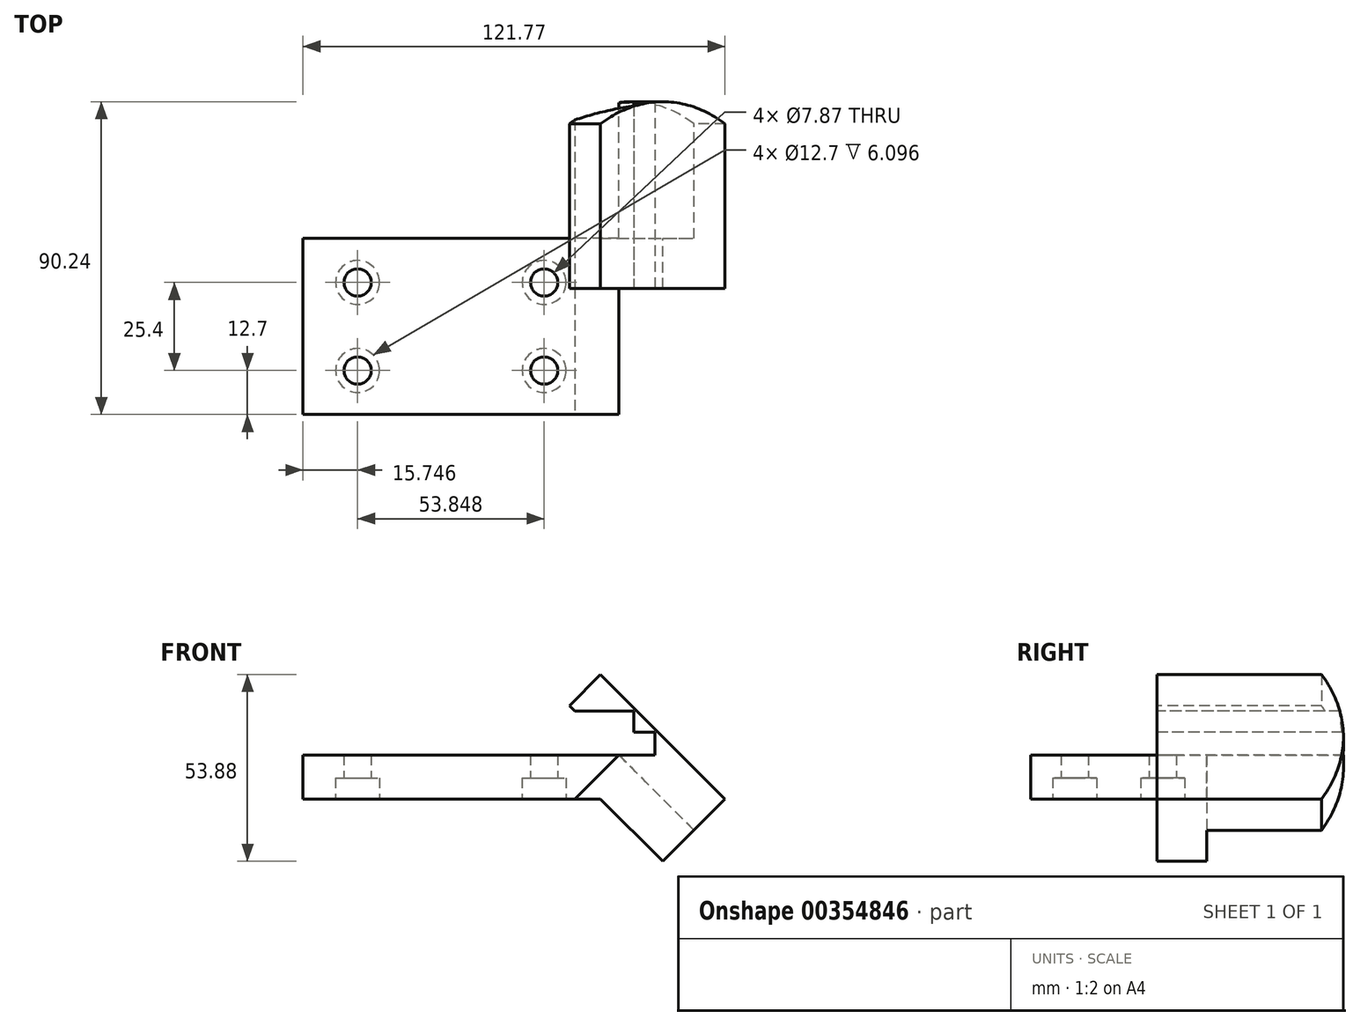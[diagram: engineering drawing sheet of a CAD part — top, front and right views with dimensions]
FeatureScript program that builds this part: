
annotation { "Feature Type Name" : "Feature", "Feature Type Description" : "" }
export const myFeature = defineFeature(function(context is Context, id is Id, definition is map)
    precondition{}
    {
        {
            var Q0;
            Q0=qCreatedBy(makeId("Front.planeOp"),FACE);
            var sketch = newSketch(context, id + "F0", { "sketchPlane" : qUnion([Q0])});
            skLineSegment(sketch, "E0.bottom", {"start": v(0, 0) * mm, "end": v(-85.85, 0) * mm});
            skLineSegment(sketch, "E0.top", {"start": v(5.26, 12.7) * mm, "end": v(-85.85, 12.7) * mm});
            skLineSegment(sketch, "E0.right", {"start": v(-85.85, 0) * mm, "end": v(-85.85, 12.7) * mm});
            skLineSegment(sketch, "E1", {"start": v(5.26, 12.7) * mm, "end": v(54.83, -36.87) * mm});
            skLineSegment(sketch, "E2", {"start": v(0, 0) * mm, "end": v(45.85, -45.85) * mm});
            skLineSegment(sketch, "E3", {"start": v(54.83, -36.87) * mm, "end": v(45.85, -45.85) * mm});
            skSolve(sketch);
        }
        {
            var Q0;
            Q0 = qSketchRegion(id + "F0", true);
            extrude(context, id + "F1", {"entities" : qUnion([Q0]), "endBound" : BoundingType.SYMMETRIC, "depth" : 50.8 * mm});
        }
        {
            var Q0;
            Q0=makeQuery(id+"F1.opExtrude","SWEPT_FACE",FACE,{"disambiguationData":[OSD([sQuery(id+"F0.wireOp",EDGE,"E0.bottom")])]});
            var sketch = newSketch(context, id + "F2", { "sketchPlane" : qUnion([Q0])});
            skPoint(sketch, "E4", {"position": v(-70.1, 12.7) * mm});
            skPoint(sketch, "E5.0.1.0", {"position": v(-70.1, -12.7) * mm});
            skPoint(sketch, "E5.1.0.0", {"position": v(-16.26, 12.7) * mm});
            skPoint(sketch, "E5.1.1.0", {"position": v(-16.26, -12.7) * mm});
            skLineSegment(sketch, "E5.direction1", {"start": v(-70.1, 12.7) * mm, "end": v(-16.26, 12.7) * mm, "construction": true});
            skLineSegment(sketch, "E5.direction2", {"start": v(-70.1, 12.7) * mm, "end": v(-70.1, -12.7) * mm, "construction": true});
            skSolve(sketch);
        }
        {
            var Q0;
            Q0=sQuery(id+"F2.wireOp",VERTEX,"E4");
            var Q1;
            Q1=sQuery(id+"F2.wireOp",VERTEX,"E5.1.0.0");
            var Q2;
            Q2=sQuery(id+"F2.wireOp",VERTEX,"E5.1.1.0");
            var Q3;
            Q3=sQuery(id+"F2.wireOp",VERTEX,"E5.0.1.0");
            var Q4;
            Q4=makeQuery(id+"F1.opExtrude","SWEPT_BODY",BODY,{"disambiguationData":[OSD([sQuery(id+"F0.wireOp",EDGE,"E0.bottom"),sQuery(id+"F0.wireOp",EDGE,"E0.top"),sQuery(id+"F0.wireOp",EDGE,"E0.right"),sQuery(id+"F0.wireOp",EDGE,"E1"),sQuery(id+"F0.wireOp",EDGE,"E2"),sQuery(id+"F0.wireOp",EDGE,"E3")])]});
            hole(context, id + "F3", {"style" : HoleStyle.C_BORE, "endStyle" : HoleEndStyle.THROUGH, "holeDiameter" : 7.87 * mm, "cBoreDiameter" : 12.7 * mm, "cBoreDepth" : 6.1 * mm, "isTappedThrough" : true, "tappedDepth" : 12.7 * mm, "tapClearance" : 3, "startFromSketch" : true, "locations" : qUnion([Q0, Q1, Q2, Q3]), "scope" : qUnion([Q4])});
        }
        {
            var Q0;
            Q0=makeQuery(id+"F1.opExtrude","SWEPT_FACE",FACE,{"disambiguationData":[OSD([sQuery(id+"F0.wireOp",EDGE,"E1")])]});
            var sketch = newSketch(context, id + "F4", { "sketchPlane" : qUnion([Q0])});
            skArc(sketch, "E6", {"start": v(58.48, -25.4) * mm, "mid": v(64.84, 0) * mm, "end": v(58.48, 25.4) * mm});
            skLineSegment(sketch, "E7.0.0", {"start": v(58.48, 25.4) * mm, "end": v(11, 25.4) * mm});
            skLineSegment(sketch, "E7.0.1", {"start": v(-5.26, 25.4) * mm, "end": v(-5.26, -25.4) * mm});
            skLineSegment(sketch, "E7.0.2", {"start": v(11, -25.4) * mm, "end": v(58.48, -25.4) * mm});
            skPoint(sketch, "E8.orphan", {"position": v(64.84, 25.4) * mm});
            skPoint(sketch, "E9.orphan", {"position": v(64.84, -25.4) * mm});
            skLineSegment(sketch, "E10", {"start": v(11, 25.4) * mm, "end": v(11, -25.4) * mm});
            skSolve(sketch);
        }
        {
            var Q0;
            Q0 = qSketchRegion(id + "F4", true);
            extrude(context, id + "F5", {"entities" : qUnion([Q0]), "operationType" : NewBodyOperationType.ADD, "depth" : 12.7 * mm});
        }
        {
            var Q0;
            {var subQ0=sQuery(id+"F0.wireOp",EDGE,"E1");var subQ1=makeQuery(id+"F1.opExtrude","SWEPT_FACE",FACE,{"disambiguationData":[OSD([subQ0])]});var subQ2=sQuery(id+"F0.wireOp",EDGE,"E3");Q0=makeQuery(id+"F5.boolean.opBoolean","SPLIT",FACE,{"disambiguationData":[TD([makeQuery(id+"F1.opExtrude","CAP_FACE",FACE,{"disambiguationData":[OSD([sQuery(id+"F0.wireOp",EDGE,"E0.bottom"),sQuery(id+"F0.wireOp",EDGE,"E0.top"),sQuery(id+"F0.wireOp",EDGE,"E0.right"),subQ0,sQuery(id+"F0.wireOp",EDGE,"E2"),subQ2])],"isStart":false}),subQ1,makeQuery(id+"F1.opExtrude","SWEPT_FACE",FACE,{"disambiguationData":[OSD([subQ2])]}),makeQuery(id+"F5.opExtrude","SWEPT_FACE",FACE,{"disambiguationData":[OSD([sQuery(id+"F4.wireOp",EDGE,"E6")])]}),makeQuery(id+"F5.opExtrude","SWEPT_FACE",FACE,{"disambiguationData":[OSD([sQuery(id+"F4.wireOp",EDGE,"E7.0.2")])]})])],"derivedFrom":subQ1});}
            var Q1;
            {var subQ0=sQuery(id+"F0.wireOp",EDGE,"E3");var subQ1=sQuery(id+"F0.wireOp",EDGE,"E1");var subQ2=makeQuery(id+"F1.opExtrude","SWEPT_FACE",FACE,{"disambiguationData":[OSD([subQ1])]});Q1=makeQuery(id+"F5.boolean.opBoolean","SPLIT",FACE,{"disambiguationData":[TD([makeQuery(id+"F1.opExtrude","CAP_FACE",FACE,{"disambiguationData":[OSD([sQuery(id+"F0.wireOp",EDGE,"E0.bottom"),sQuery(id+"F0.wireOp",EDGE,"E0.top"),sQuery(id+"F0.wireOp",EDGE,"E0.right"),subQ1,sQuery(id+"F0.wireOp",EDGE,"E2"),subQ0])],"isStart":true}),subQ2,makeQuery(id+"F1.opExtrude","SWEPT_FACE",FACE,{"disambiguationData":[OSD([subQ0])]}),makeQuery(id+"F5.opExtrude","SWEPT_FACE",FACE,{"disambiguationData":[OSD([sQuery(id+"F4.wireOp",EDGE,"E6")])]}),makeQuery(id+"F5.opExtrude","SWEPT_FACE",FACE,{"disambiguationData":[OSD([sQuery(id+"F4.wireOp",EDGE,"E7.0.0")])]})])],"derivedFrom":subQ2});}
            extrude(context, id + "F6", {"entities" : qUnion([Q0, Q1]), "operationType" : NewBodyOperationType.REMOVE, "endBound" : BoundingType.THROUGH_ALL, "oppositeDirection" : true, "depth" : 25.4 * mm});
        }
        {
            var Q0;
            Q0=makeQuery(id+"F5.opExtrude","SWEPT_FACE",FACE,{"disambiguationData":[OSD([sQuery(id+"F4.wireOp",EDGE,"E10")])]});
            var sketch = newSketch(context, id + "F7", { "sketchPlane" : qUnion([Q0])});
            skLineSegment(sketch, "E11.0.0", {"start": v(-25.4, 12.7) * mm, "end": v(25.4, 12.7) * mm});
            skLineSegment(sketch, "E11.0.1", {"start": v(25.4, 12.7) * mm, "end": v(25.4, 25.4) * mm});
            skLineSegment(sketch, "E11.0.2", {"start": v(9.65, 25.4) * mm, "end": v(-9.65, 25.4) * mm});
            skLineSegment(sketch, "E11.0.3", {"start": v(-25.4, 25.4) * mm, "end": v(-25.4, 12.7) * mm});
            skLineSegment(sketch, "E12.bottom", {"start": v(-15.75, 12.7) * mm, "end": v(15.75, 12.7) * mm});
            skLineSegment(sketch, "E12.top", {"start": v(-15.75, 19.3) * mm, "end": v(15.75, 19.3) * mm});
            skLineSegment(sketch, "E12.left", {"start": v(-15.75, 12.7) * mm, "end": v(-15.75, 19.3) * mm});
            skLineSegment(sketch, "E12.right", {"start": v(15.75, 12.7) * mm, "end": v(15.75, 19.3) * mm});
            skLineSegment(sketch, "E13", {"start": v(-9.65, 19.3) * mm, "end": v(-9.65, 25.4) * mm});
            skLineSegment(sketch, "E14", {"start": v(9.65, 19.3) * mm, "end": v(9.65, 25.4) * mm});
            skSolve(sketch);
        }
        {
            var Q0;
            Q0 = qSketchRegion(id + "F7", true);
            extrude(context, id + "F8", {"entities" : qUnion([Q0]), "operationType" : NewBodyOperationType.REMOVE, "endBound" : BoundingType.THROUGH_ALL, "oppositeDirection" : true, "depth" : 25.4 * mm});
        }
    });
